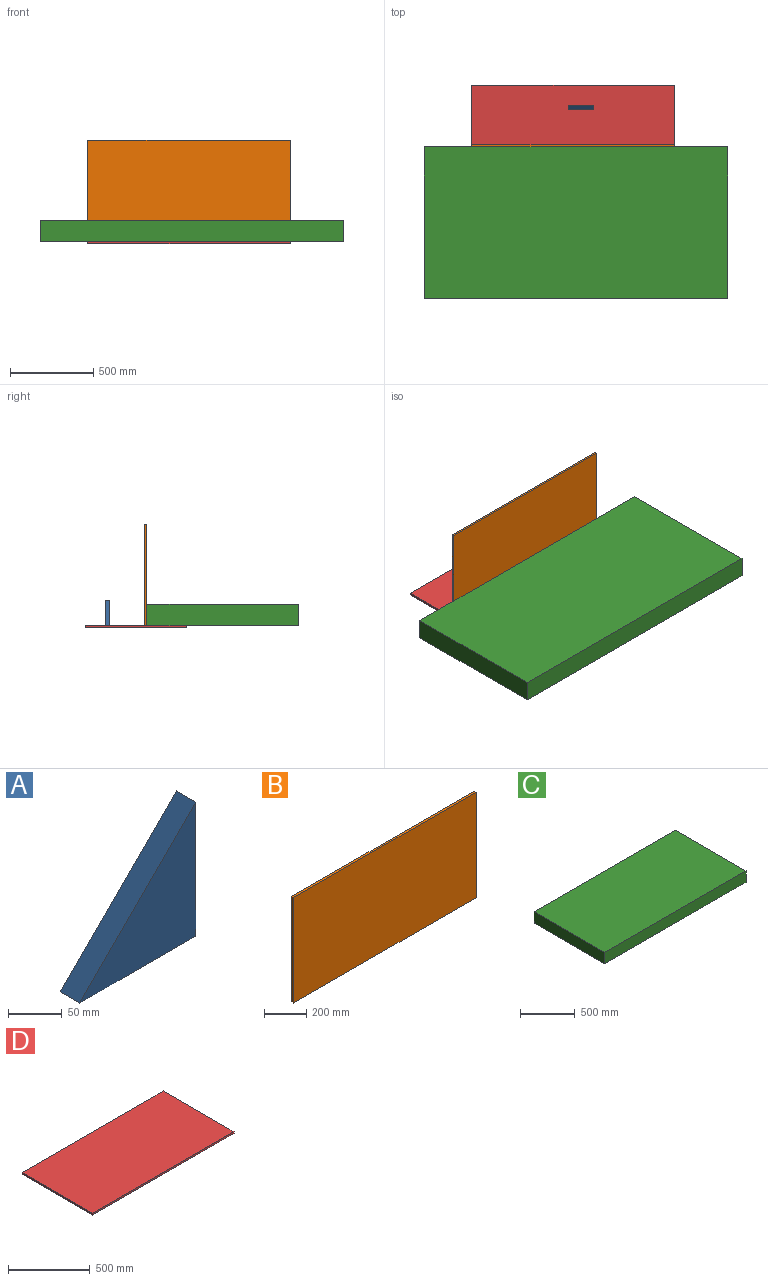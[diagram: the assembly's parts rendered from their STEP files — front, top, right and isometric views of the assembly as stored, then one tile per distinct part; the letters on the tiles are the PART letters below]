
ASSEMBLY  parts=4 mates=5
PART A: 5 faces, bbox 152.4x25.4x152.4 mm
  f0: plane 152.4x25.4mm, normal (0,0,-1), area 3871mm2, adj f1,f2,f3,f4
  f1: plane 152.4x25.4mm, normal (1,0,0), area 3871mm2, adj f0,f2,f3,f4
  f2: plane 152.4x152.4mm, normal (-0.71,0,0.71), area 5474.4mm2, adj f0,f1,f3,f4
  f3: plane 152.4x152.4mm, normal (0,-1,0), area 11612.9mm2, adj f0,f1,f2
  f4: plane 152.4x152.4mm, normal (0,1,0), area 11612.9mm2, adj f0,f1,f2
PART B: 6 faces, bbox 1219.2x12.7x609.6 mm
  f0: plane 1219.2x12.7mm, normal (0,0,-1), area 15483.8mm2, adj f1,f3,f4,f5
  f1: plane 609.6x12.7mm, normal (1,0,0), area 7741.9mm2, adj f0,f2,f4,f5
  f2: plane 1219.2x12.7mm, normal (0,0,1), area 15483.8mm2, adj f1,f3,f4,f5
  f3: plane 609.6x12.7mm, normal (-1,0,0), area 7741.9mm2, adj f0,f2,f4,f5
  f4: plane 1219.2x609.6mm, normal (0,-1,0), area 743224.3mm2, adj f0,f1,f2,f3
  f5: plane 1219.2x609.6mm, normal (0,1,0), area 743224.3mm2, adj f0,f1,f2,f3
PART C: 6 faces, bbox 1828.8x914.4x127 mm
  f0: plane 1828.8x127mm, normal (0,-1,0), area 232257.6mm2, adj f1,f3,f4,f5
  f1: plane 914.4x127mm, normal (1,0,0), area 116128.8mm2, adj f0,f2,f4,f5
  f2: plane 1828.8x127mm, normal (0,1,0), area 232257.6mm2, adj f1,f3,f4,f5
  f3: plane 914.4x127mm, normal (-1,0,0), area 116128.8mm2, adj f0,f2,f4,f5
  f4: plane 1828.8x914.4mm, normal (0,0,1), area 1672254.7mm2, adj f0,f1,f2,f3
  f5: plane 1828.8x914.4mm, normal (0,0,-1), area 1672254.7mm2, adj f0,f1,f2,f3
PART D: 6 faces, bbox 1219.2x609.6x12.7 mm
  f0: plane 1219.2x12.7mm, normal (0,-1,0), area 15483.8mm2, adj f1,f3,f4,f5
  f1: plane 609.6x12.7mm, normal (1,0,0), area 7741.9mm2, adj f0,f2,f4,f5
  f2: plane 1219.2x12.7mm, normal (0,1,0), area 15483.8mm2, adj f1,f3,f4,f5
  f3: plane 609.6x12.7mm, normal (-1,0,0), area 7741.9mm2, adj f0,f2,f4,f5
  f4: plane 1219.2x609.6mm, normal (0,0,1), area 743224.3mm2, adj f0,f1,f2,f3
  f5: plane 1219.2x609.6mm, normal (0,0,-1), area 743224.3mm2, adj f0,f1,f2,f3
PLACE A t=(-38.81,425.59,424.7)mm
PLACE B t=(-161.66,195.68,729.5)mm
PLACE C t=(-144.21,-267.87,488.2)mm
PLACE D t=(-162,255.46,418.35)mm
MATE parallel D.f1 <-> B.f1  axis (1,0,0) through (447.6,255.46,418.35)mm
MATE planar D.f4 <-> C.f5  axis (0,0,1) through (-162,255.46,424.7)mm
MATE planar D.f4 <-> B.f0  axis (0,0,1) through (-162,560.26,424.7)mm
MATE planar A.f0 <-> D.f4  axis (0,0,-1) through (-115.01,412.89,424.7)mm
MATE planar B.f4 <-> C.f2  axis (0,-1,0) through (-161.66,189.33,729.5)mm
